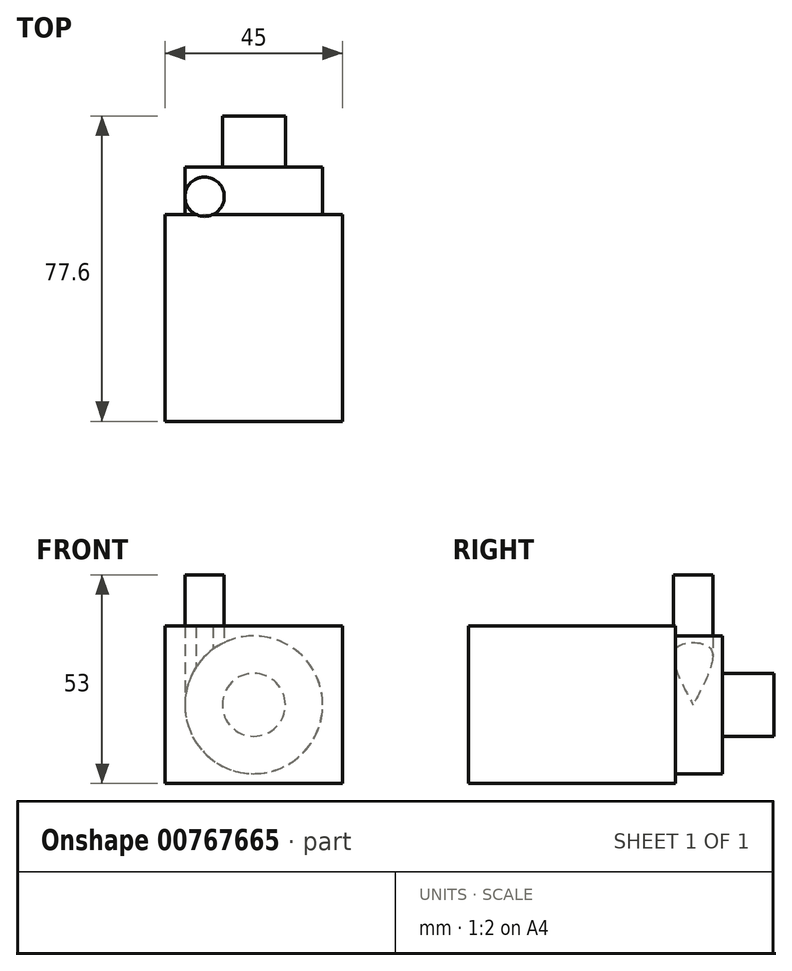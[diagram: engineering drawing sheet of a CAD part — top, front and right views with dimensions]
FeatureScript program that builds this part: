
annotation { "Feature Type Name" : "Feature", "Feature Type Description" : "" }
export const myFeature = defineFeature(function(context is Context, id is Id, definition is map)
    precondition{}
    {
        {
            var Q0;
            Q0=qCreatedBy(makeId("Front.planeOp"),FACE);
            var sketch = newSketch(context, id + "F0", { "sketchPlane" : qUnion([Q0])});
            skLineSegment(sketch, "E0.bottom", {"start": v(22.5, -20) * mm, "end": v(-22.5, -20) * mm});
            skLineSegment(sketch, "E0.top", {"start": v(22.5, 20) * mm, "end": v(-22.5, 20) * mm});
            skLineSegment(sketch, "E0.left", {"start": v(22.5, -20) * mm, "end": v(22.5, 20) * mm});
            skLineSegment(sketch, "E0.right", {"start": v(-22.5, -20) * mm, "end": v(-22.5, 20) * mm});
            skPoint(sketch, "E0.middle", {"position": v(0, 0) * mm});
            skCircle(sketch, "E1", {"center": v(0, 0) * mm, "radius": 17.5 * mm});
            skCircle(sketch, "E2", {"center": v(0, 0) * mm, "radius": 8 * mm});
            skSolve(sketch);
        }
        {
            var Q0;
            Q0 = qSketchRegion(id + "F0", true);
            var Q1;
            Q1=makeQuery(id+"F0.imprint","IMPRINT",FACE,{"disambiguationData":[TD([[makeQuery(id+"F0.imprint","IMPRINT",EDGE,{"derivedFrom":sQuery(id+"F0.wireOp",EDGE,"E1")}),1.0]])]});
            var Q2;
            Q2=makeQuery(id+"F0.imprint","IMPRINT",FACE,{"disambiguationData":[TD([[makeQuery(id+"F0.imprint","IMPRINT",EDGE,{"derivedFrom":sQuery(id+"F0.wireOp",EDGE,"E2")}),1.0]])]});
            extrude(context, id + "F1", {"entities" : qUnion([Q0, Q1, Q2]), "depth" : 52.6 * mm, "offsetDistance" : 25 * mm});
        }
        {
            var Q0;
            Q0=makeQuery(id+"F0.imprint","IMPRINT",FACE,{"disambiguationData":[TD([[makeQuery(id+"F0.imprint","IMPRINT",EDGE,{"derivedFrom":sQuery(id+"F0.wireOp",EDGE,"E1")}),1.0]])]});
            extrude(context, id + "F2", {"entities" : qUnion([Q0]), "operationType" : NewBodyOperationType.ADD, "oppositeDirection" : true, "depth" : 12 * mm, "offsetDistance" : 25 * mm});
        }
        {
            var Q0;
            Q0=makeQuery(id+"F0.imprint","IMPRINT",FACE,{"disambiguationData":[TD([[makeQuery(id+"F0.imprint","IMPRINT",EDGE,{"derivedFrom":sQuery(id+"F0.wireOp",EDGE,"E2")}),1.0]])]});
            extrude(context, id + "F3", {"entities" : qUnion([Q0]), "operationType" : NewBodyOperationType.ADD, "oppositeDirection" : true, "depth" : 25 * mm, "offsetDistance" : 25 * mm});
        }
        {
            var Q0;
            Q0=qCreatedBy(makeId("Top.planeOp"),FACE);
            var sketch = newSketch(context, id + "F4", { "sketchPlane" : qUnion([Q0])});
            skCircle(sketch, "E3", {"center": v(-12.5, 4.5) * mm, "radius": 5 * mm});
            skSolve(sketch);
        }
        {
            var Q0;
            Q0 = qSketchRegion(id + "F4", true);
            extrude(context, id + "F5", {"entities" : qUnion([Q0]), "operationType" : NewBodyOperationType.ADD, "depth" : 33 * mm, "offsetDistance" : 25 * mm});
        }
    });
